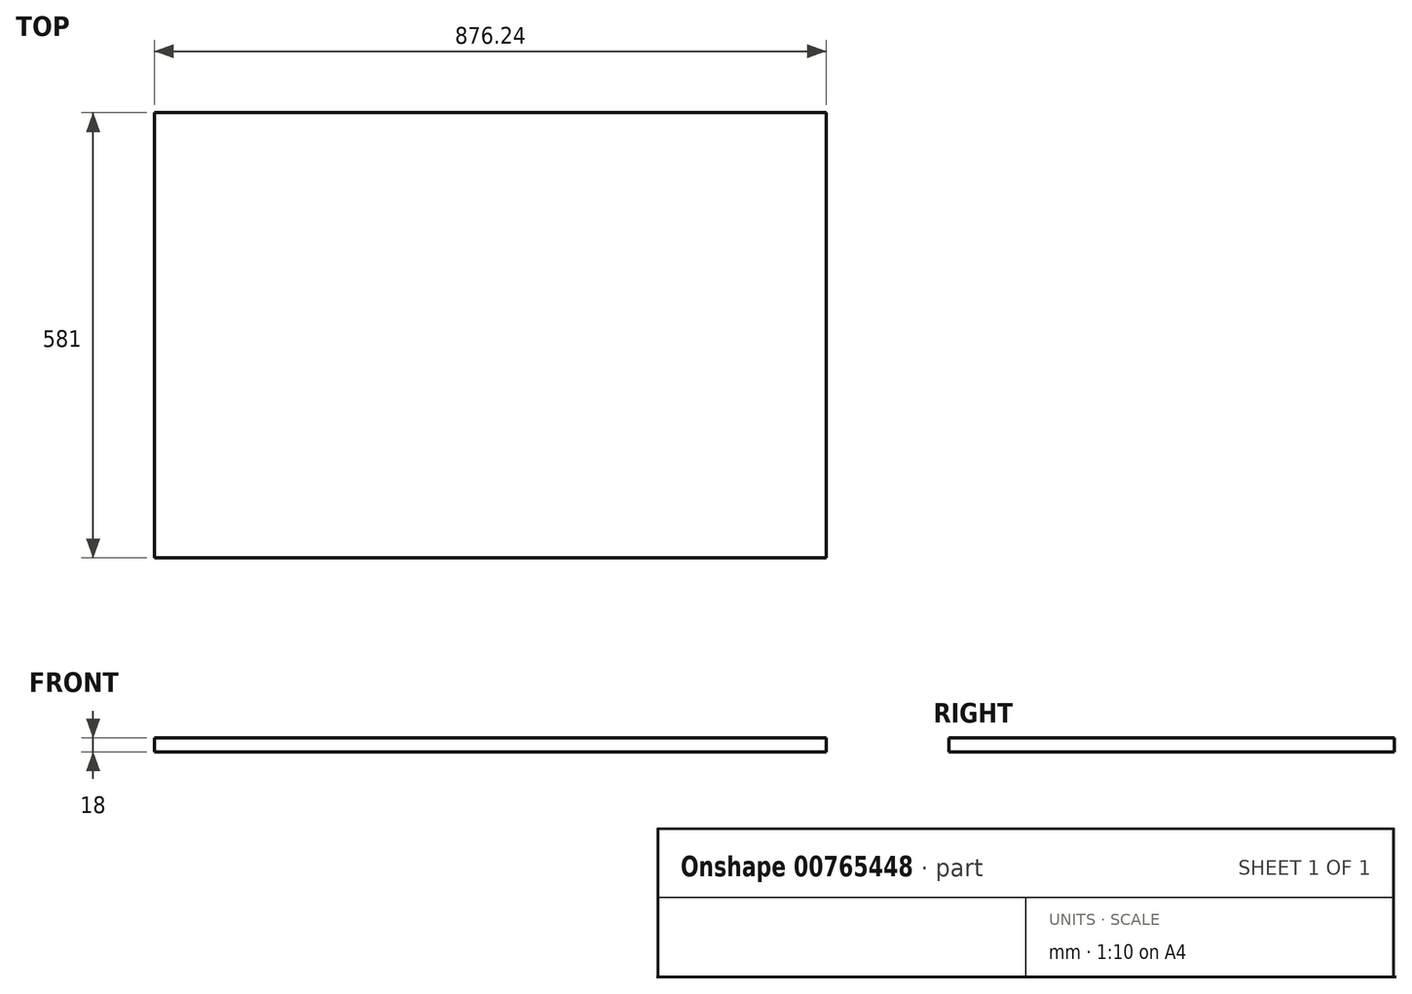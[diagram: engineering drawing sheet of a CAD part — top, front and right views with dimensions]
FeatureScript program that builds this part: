
annotation { "Feature Type Name" : "Feature", "Feature Type Description" : "" }
export const myFeature = defineFeature(function(context is Context, id is Id, definition is map)
    precondition{}
    {
        {
            var Q0;
            Q0=qCreatedBy(makeId("Top.planeOp"),FACE);
            var sketch = newSketch(context, id + "F0", { "sketchPlane" : qUnion([Q0])});
            skLineSegment(sketch, "E0.bottom", {"start": v(-438.12, -290.5) * mm, "end": v(438.13, -290.5) * mm});
            skLineSegment(sketch, "E0.top", {"start": v(-438.13, 290.5) * mm, "end": v(438.12, 290.5) * mm});
            skLineSegment(sketch, "E0.left", {"start": v(-438.12, -290.5) * mm, "end": v(-438.13, 290.5) * mm});
            skLineSegment(sketch, "E0.right", {"start": v(438.13, -290.5) * mm, "end": v(438.12, 290.5) * mm});
            skPoint(sketch, "E0.middle", {"position": v(0, 0) * mm});
            skSolve(sketch);
        }
        {
            var Q0;
            Q0 = qSketchRegion(id + "F0", true);
            extrude(context, id + "F1", {"entities" : qUnion([Q0]), "depth" : 18 * mm, "offsetDistance" : 25 * mm});
        }
    });
